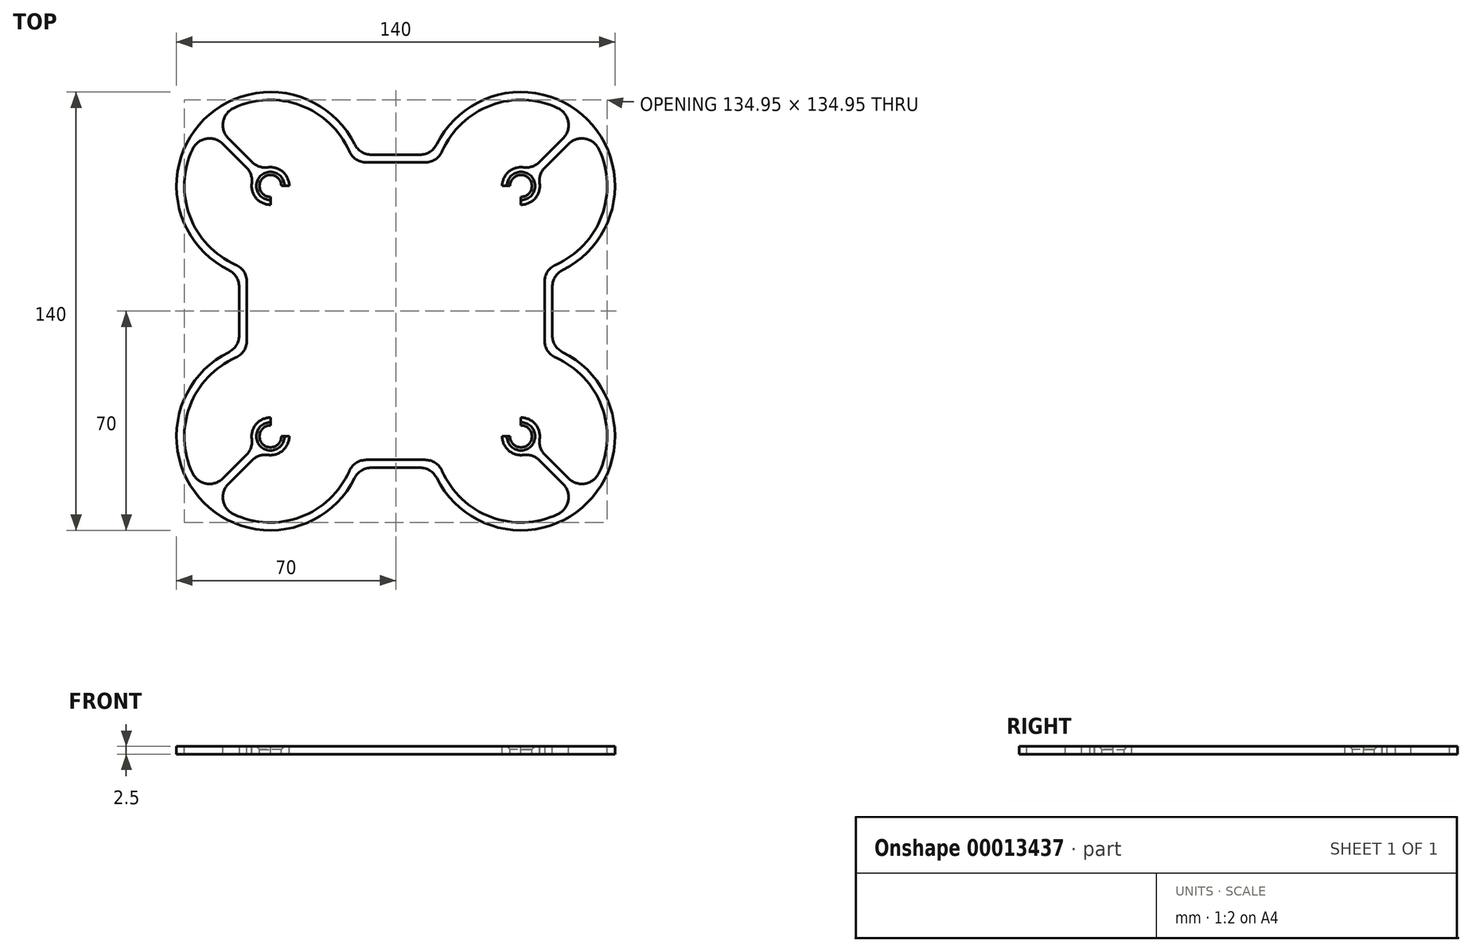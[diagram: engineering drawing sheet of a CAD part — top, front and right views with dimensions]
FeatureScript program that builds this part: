
annotation { "Feature Type Name" : "Feature", "Feature Type Description" : "" }
export const myFeature = defineFeature(function(context is Context, id is Id, definition is map)
    precondition{}
    {
        {
            var Q0;
            Q0=qCreatedBy(makeId("Top.planeOp"),FACE);
            var sketch = newSketch(context, id + "F0", { "sketchPlane" : qUnion([Q0])});
            skLineSegment(sketch, "E0.rect.bottom", {"start": v(40, 40) * mm, "end": v(-40, 40) * mm});
            skLineSegment(sketch, "E0.rect.top", {"start": v(40, -40) * mm, "end": v(-40, -40) * mm});
            skLineSegment(sketch, "E0.rect.left", {"start": v(40, 40) * mm, "end": v(40, -40) * mm});
            skLineSegment(sketch, "E0.rect.right", {"start": v(-40, 40) * mm, "end": v(-40, -40) * mm});
            skPoint(sketch, "E0.rect.middle", {"position": v(0, 0) * mm});
            skCircle(sketch, "E1", {"center": v(40, 40) * mm, "radius": 3.5 * mm});
            skCircle(sketch, "E2", {"center": v(-40, 40) * mm, "radius": 3.5 * mm});
            skCircle(sketch, "E3", {"center": v(-40, -40) * mm, "radius": 3.5 * mm});
            skCircle(sketch, "E4", {"center": v(40, -40) * mm, "radius": 3.5 * mm});
            skCircle(sketch, "E5", {"center": v(-40, -40) * mm, "radius": 30 * mm});
            skCircle(sketch, "E6", {"center": v(-40, 40) * mm, "radius": 30 * mm});
            skCircle(sketch, "E7", {"center": v(40, 40) * mm, "radius": 30 * mm});
            skCircle(sketch, "E8", {"center": v(40, -40) * mm, "radius": 30 * mm});
            skCircle(sketch, "E9", {"center": v(-40, 40) * mm, "radius": 27.5 * mm});
            skCircle(sketch, "E10", {"center": v(-40, -40) * mm, "radius": 27.5 * mm});
            skCircle(sketch, "E11", {"center": v(40, 40) * mm, "radius": 27.5 * mm});
            skCircle(sketch, "E12", {"center": v(40, -40) * mm, "radius": 27.5 * mm});
            skLineSegment(sketch, "E13", {"start": v(-40, 67.5) * mm, "end": v(-40, 70) * mm, "construction": true});
            skLineSegment(sketch, "E14", {"start": v(-40, -67.5) * mm, "end": v(-40, -70) * mm, "construction": true});
            skLineSegment(sketch, "E15", {"start": v(40, -67.5) * mm, "end": v(40, -70) * mm, "construction": true});
            skLineSegment(sketch, "E16", {"start": v(40, 67.5) * mm, "end": v(40, 70) * mm, "construction": true});
            skLineSegment(sketch, "E17.rect.bottom", {"start": v(50, 50) * mm, "end": v(-50, 50) * mm});
            skLineSegment(sketch, "E17.rect.top", {"start": v(50, -50) * mm, "end": v(-50, -50) * mm});
            skLineSegment(sketch, "E17.rect.left", {"start": v(50, 50) * mm, "end": v(50, -50) * mm});
            skLineSegment(sketch, "E17.rect.right", {"start": v(-50, 50) * mm, "end": v(-50, -50) * mm});
            skLineSegment(sketch, "E18.rect.bottom", {"start": v(47.5, 47.5) * mm, "end": v(-47.5, 47.5) * mm});
            skLineSegment(sketch, "E18.rect.top", {"start": v(47.5, -47.5) * mm, "end": v(-47.5, -47.5) * mm});
            skLineSegment(sketch, "E18.rect.left", {"start": v(47.5, 47.5) * mm, "end": v(47.5, -47.5) * mm});
            skLineSegment(sketch, "E18.rect.right", {"start": v(-47.5, 47.5) * mm, "end": v(-47.5, -47.5) * mm});
            skLineSegment(sketch, "E19", {"start": v(0, 47.5) * mm, "end": v(0, 50) * mm, "construction": true});
            skLineSegment(sketch, "E20", {"start": v(-40, -40) * mm, "end": v(-59.45, -59.45) * mm, "construction": true});
            skLineSegment(sketch, "E21", {"start": v(-60.3, -58.54) * mm, "end": v(-45.03, -43.27) * mm});
            skLineSegment(sketch, "E22", {"start": v(-52.67, -50.9) * mm, "end": v(-50.9, -52.67) * mm, "construction": true});
            skLineSegment(sketch, "E23", {"start": v(-40, 40) * mm, "end": v(-59.45, 59.45) * mm, "construction": true});
            skCircle(sketch, "E24", {"center": v(-40, -40) * mm, "radius": 6 * mm});
            skLineSegment(sketch, "E25", {"start": v(-43.5, -40) * mm, "end": v(-46, -40) * mm, "construction": true});
            skLineSegment(sketch, "E26", {"start": v(-43.27, -45.03) * mm, "end": v(-58.54, -60.3) * mm});
            skCircle(sketch, "E27", {"center": v(-40, 40) * mm, "radius": 6 * mm});
            skLineSegment(sketch, "E28", {"start": v(-40, 43.5) * mm, "end": v(-40, 46) * mm, "construction": true});
            skLineSegment(sketch, "E29", {"start": v(-45.03, 43.27) * mm, "end": v(-60.3, 58.54) * mm});
            skLineSegment(sketch, "E30", {"start": v(-43.27, 45.03) * mm, "end": v(-58.54, 60.3) * mm});
            skLineSegment(sketch, "E31", {"start": v(-52.67, 50.9) * mm, "end": v(-50.9, 52.67) * mm, "construction": true});
            skLineSegment(sketch, "E32", {"start": v(40, 40) * mm, "end": v(61.21, 61.21) * mm, "construction": true});
            skLineSegment(sketch, "E33", {"start": v(50.9, 52.67) * mm, "end": v(52.67, 50.9) * mm, "construction": true});
            skCircle(sketch, "E34", {"center": v(40, 40) * mm, "radius": 6 * mm});
            skLineSegment(sketch, "E35", {"start": v(40, 43.5) * mm, "end": v(40, 46) * mm, "construction": true});
            skLineSegment(sketch, "E36", {"start": v(45.03, 43.27) * mm, "end": v(60.3, 58.54) * mm});
            skLineSegment(sketch, "E37", {"start": v(43.27, 45.03) * mm, "end": v(58.54, 60.3) * mm});
            skCircle(sketch, "E38", {"center": v(40, -40) * mm, "radius": 6 * mm});
            skLineSegment(sketch, "E39", {"start": v(40, -43.5) * mm, "end": v(40, -46) * mm, "construction": true});
            skLineSegment(sketch, "E40", {"start": v(40, -40) * mm, "end": v(59.45, -59.45) * mm, "construction": true});
            skLineSegment(sketch, "E41", {"start": v(43.27, -45.03) * mm, "end": v(58.54, -60.3) * mm});
            skLineSegment(sketch, "E42", {"start": v(45.03, -43.27) * mm, "end": v(60.3, -58.54) * mm});
            skLineSegment(sketch, "E43", {"start": v(50.9, -52.67) * mm, "end": v(52.67, -50.9) * mm, "construction": true});
            skSolve(sketch);
        }
        {
            var Q0;
            {var subQ3=sQuery(id+"F0.wireOp",EDGE,"E6");var subQ5=sQuery(id+"F0.wireOp",EDGE,"E17.rect.bottom");var subQ7=makeQuery(id+"F0.imprint","INTERSECT",VERTEX,{"derivedFrom":[subQ3,subQ5]});Q0=makeQuery(id+"F0.imprint","IMPRINT",FACE,{"disambiguationData":[TD([[makeQuery(id+"F0.imprint","IMPRINT",EDGE,{"disambiguationData":[TD([[subQ7,-1.0]])],"derivedFrom":subQ3}),1.0]])]});}
            var Q1;
            {var subQ3=sQuery(id+"F0.wireOp",EDGE,"E5");var subQ5=sQuery(id+"F0.wireOp",EDGE,"E17.rect.right");var subQ7=makeQuery(id+"F0.imprint","INTERSECT",VERTEX,{"derivedFrom":[subQ3,subQ5]});Q1=makeQuery(id+"F0.imprint","IMPRINT",FACE,{"disambiguationData":[TD([[makeQuery(id+"F0.imprint","IMPRINT",EDGE,{"disambiguationData":[TD([[subQ7,1.0]])],"derivedFrom":subQ3}),-1.0]])]});}
            var Q2;
            {var subQ0=sQuery(id+"F0.wireOp",EDGE,"E17.rect.right");var subQ3=sQuery(id+"F0.wireOp",EDGE,"E6");var subQ4=makeQuery(id+"F0.imprint","INTERSECT",VERTEX,{"derivedFrom":[subQ3,subQ0]});Q2=makeQuery(id+"F0.imprint","IMPRINT",FACE,{"disambiguationData":[TD([[makeQuery(id+"F0.imprint","IMPRINT",EDGE,{"disambiguationData":[TD([[subQ4,-1.0]])],"derivedFrom":subQ3}),1.0]])]});}
            var Q3;
            {var subQ3=sQuery(id+"F0.wireOp",EDGE,"E6");var subQ5=sQuery(id+"F0.wireOp",EDGE,"E17.rect.bottom");var subQ7=makeQuery(id+"F0.imprint","INTERSECT",VERTEX,{"derivedFrom":[subQ3,subQ5]});Q3=makeQuery(id+"F0.imprint","IMPRINT",FACE,{"disambiguationData":[TD([[makeQuery(id+"F0.imprint","IMPRINT",EDGE,{"disambiguationData":[TD([[subQ7,1.0]])],"derivedFrom":subQ3}),1.0]])]});}
            var Q4;
            {var subQ1=sQuery(id+"F0.wireOp",EDGE,"E18.rect.bottom");var subQ6=sQuery(id+"F0.wireOp",EDGE,"E18.rect.right");var subQ9=makeQuery(id+"F0.imprint","INTERSECT",VERTEX,{"derivedFrom":[subQ1,subQ6]});Q4=makeQuery(id+"F0.imprint","IMPRINT",FACE,{"disambiguationData":[TD([[makeQuery(id+"F0.imprint","IMPRINT",EDGE,{"disambiguationData":[TD([[subQ9,1.0]])],"derivedFrom":subQ1}),1.0]])]});}
            var Q5;
            {var subQ3=sQuery(id+"F0.wireOp",EDGE,"E17.rect.bottom");var subQ8=sQuery(id+"F0.wireOp",EDGE,"E17.rect.right");var subQ11=makeQuery(id+"F0.imprint","INTERSECT",VERTEX,{"derivedFrom":[subQ3,subQ8]});Q5=makeQuery(id+"F0.imprint","IMPRINT",FACE,{"disambiguationData":[TD([[makeQuery(id+"F0.imprint","IMPRINT",EDGE,{"disambiguationData":[TD([[subQ11,1.0]])],"derivedFrom":subQ3}),1.0]])]});}
            var Q6;
            {var subQ0=sQuery(id+"F0.wireOp",EDGE,"E29");var subQ3=sQuery(id+"F0.wireOp",EDGE,"E9");var subQ4=makeQuery(id+"F0.imprint","INTERSECT",VERTEX,{"derivedFrom":[subQ3,subQ0]});Q6=makeQuery(id+"F0.imprint","IMPRINT",FACE,{"disambiguationData":[TD([[makeQuery(id+"F0.imprint","IMPRINT",EDGE,{"disambiguationData":[TD([[subQ4,1.0]])],"derivedFrom":subQ3}),1.0]])]});}
            var Q7;
            {var subQ3=sQuery(id+"F0.wireOp",EDGE,"E6");var subQ5=sQuery(id+"F0.wireOp",EDGE,"E17.rect.bottom");var subQ7=makeQuery(id+"F0.imprint","INTERSECT",VERTEX,{"derivedFrom":[subQ3,subQ5]});Q7=makeQuery(id+"F0.imprint","IMPRINT",FACE,{"disambiguationData":[TD([[makeQuery(id+"F0.imprint","IMPRINT",EDGE,{"disambiguationData":[TD([[subQ7,1.0]])],"derivedFrom":subQ3}),-1.0]])]});}
            var Q8;
            {var subQ3=sQuery(id+"F0.wireOp",EDGE,"E7");var subQ5=sQuery(id+"F0.wireOp",EDGE,"E17.rect.bottom");var subQ7=makeQuery(id+"F0.imprint","INTERSECT",VERTEX,{"derivedFrom":[subQ3,subQ5]});Q8=makeQuery(id+"F0.imprint","IMPRINT",FACE,{"disambiguationData":[TD([[makeQuery(id+"F0.imprint","IMPRINT",EDGE,{"disambiguationData":[TD([[subQ7,-1.0]])],"derivedFrom":subQ3}),1.0]])]});}
            var Q9;
            {var subQ3=sQuery(id+"F0.wireOp",EDGE,"E7");var subQ5=sQuery(id+"F0.wireOp",EDGE,"E17.rect.bottom");var subQ7=makeQuery(id+"F0.imprint","INTERSECT",VERTEX,{"derivedFrom":[subQ3,subQ5]});Q9=makeQuery(id+"F0.imprint","IMPRINT",FACE,{"disambiguationData":[TD([[makeQuery(id+"F0.imprint","IMPRINT",EDGE,{"disambiguationData":[TD([[subQ7,1.0]])],"derivedFrom":subQ3}),1.0]])]});}
            var Q10;
            {var subQ3=sQuery(id+"F0.wireOp",EDGE,"E11");var subQ5=sQuery(id+"F0.wireOp",EDGE,"E36");var subQ8=makeQuery(id+"F0.imprint","INTERSECT",VERTEX,{"derivedFrom":[subQ3,subQ5]});Q10=makeQuery(id+"F0.imprint","IMPRINT",FACE,{"disambiguationData":[TD([[makeQuery(id+"F0.imprint","IMPRINT",EDGE,{"disambiguationData":[TD([[subQ8,-1.0]])],"derivedFrom":subQ3}),1.0]])]});}
            var Q11;
            {var subQ3=sQuery(id+"F0.wireOp",EDGE,"E17.rect.bottom");var subQ8=sQuery(id+"F0.wireOp",EDGE,"E17.rect.left");var subQ11=makeQuery(id+"F0.imprint","INTERSECT",VERTEX,{"derivedFrom":[subQ3,subQ8]});Q11=makeQuery(id+"F0.imprint","IMPRINT",FACE,{"disambiguationData":[TD([[makeQuery(id+"F0.imprint","IMPRINT",EDGE,{"disambiguationData":[TD([[subQ11,-1.0]])],"derivedFrom":subQ3}),1.0]])]});}
            var Q12;
            {var subQ1=sQuery(id+"F0.wireOp",EDGE,"E18.rect.bottom");var subQ6=sQuery(id+"F0.wireOp",EDGE,"E18.rect.left");var subQ9=makeQuery(id+"F0.imprint","INTERSECT",VERTEX,{"derivedFrom":[subQ1,subQ6]});Q12=makeQuery(id+"F0.imprint","IMPRINT",FACE,{"disambiguationData":[TD([[makeQuery(id+"F0.imprint","IMPRINT",EDGE,{"disambiguationData":[TD([[subQ9,-1.0]])],"derivedFrom":subQ1}),1.0]])]});}
            var Q13;
            {var subQ3=sQuery(id+"F0.wireOp",EDGE,"E7");var subQ5=sQuery(id+"F0.wireOp",EDGE,"E17.rect.left");var subQ7=makeQuery(id+"F0.imprint","INTERSECT",VERTEX,{"derivedFrom":[subQ3,subQ5]});Q13=makeQuery(id+"F0.imprint","IMPRINT",FACE,{"disambiguationData":[TD([[makeQuery(id+"F0.imprint","IMPRINT",EDGE,{"disambiguationData":[TD([[subQ7,1.0]])],"derivedFrom":subQ3}),-1.0]])]});}
            var Q14;
            {var subQ3=sQuery(id+"F0.wireOp",EDGE,"E8");var subQ5=sQuery(id+"F0.wireOp",EDGE,"E17.rect.left");var subQ7=makeQuery(id+"F0.imprint","INTERSECT",VERTEX,{"derivedFrom":[subQ3,subQ5]});Q14=makeQuery(id+"F0.imprint","IMPRINT",FACE,{"disambiguationData":[TD([[makeQuery(id+"F0.imprint","IMPRINT",EDGE,{"disambiguationData":[TD([[subQ7,-1.0]])],"derivedFrom":subQ3}),1.0]])]});}
            var Q15;
            {var subQ0=sQuery(id+"F0.wireOp",EDGE,"E17.rect.left");var subQ3=sQuery(id+"F0.wireOp",EDGE,"E7");var subQ4=makeQuery(id+"F0.imprint","INTERSECT",VERTEX,{"derivedFrom":[subQ3,subQ0]});Q15=makeQuery(id+"F0.imprint","IMPRINT",FACE,{"disambiguationData":[TD([[makeQuery(id+"F0.imprint","IMPRINT",EDGE,{"disambiguationData":[TD([[subQ4,1.0]])],"derivedFrom":subQ3}),1.0]])]});}
            var Q16;
            {var subQ3=sQuery(id+"F0.wireOp",EDGE,"E17.rect.left");var subQ8=sQuery(id+"F0.wireOp",EDGE,"E17.rect.top");var subQ11=makeQuery(id+"F0.imprint","INTERSECT",VERTEX,{"derivedFrom":[subQ8,subQ3]});Q16=makeQuery(id+"F0.imprint","IMPRINT",FACE,{"disambiguationData":[TD([[makeQuery(id+"F0.imprint","IMPRINT",EDGE,{"disambiguationData":[TD([[subQ11,-1.0]])],"derivedFrom":subQ8}),-1.0]])]});}
            var Q17;
            {var subQ0=sQuery(id+"F0.wireOp",EDGE,"E17.rect.left");var subQ3=sQuery(id+"F0.wireOp",EDGE,"E8");var subQ4=makeQuery(id+"F0.imprint","INTERSECT",VERTEX,{"derivedFrom":[subQ3,subQ0]});Q17=makeQuery(id+"F0.imprint","IMPRINT",FACE,{"disambiguationData":[TD([[makeQuery(id+"F0.imprint","IMPRINT",EDGE,{"disambiguationData":[TD([[subQ4,1.0]])],"derivedFrom":subQ3}),1.0]])]});}
            var Q18;
            {var subQ3=sQuery(id+"F0.wireOp",EDGE,"E12");var subQ5=sQuery(id+"F0.wireOp",EDGE,"E41");var subQ8=makeQuery(id+"F0.imprint","INTERSECT",VERTEX,{"derivedFrom":[subQ3,subQ5]});Q18=makeQuery(id+"F0.imprint","IMPRINT",FACE,{"disambiguationData":[TD([[makeQuery(id+"F0.imprint","IMPRINT",EDGE,{"disambiguationData":[TD([[subQ8,-1.0]])],"derivedFrom":subQ3}),1.0]])]});}
            var Q19;
            {var subQ1=sQuery(id+"F0.wireOp",EDGE,"E18.rect.left");var subQ6=sQuery(id+"F0.wireOp",EDGE,"E18.rect.top");var subQ9=makeQuery(id+"F0.imprint","INTERSECT",VERTEX,{"derivedFrom":[subQ6,subQ1]});Q19=makeQuery(id+"F0.imprint","IMPRINT",FACE,{"disambiguationData":[TD([[makeQuery(id+"F0.imprint","IMPRINT",EDGE,{"disambiguationData":[TD([[subQ9,-1.0]])],"derivedFrom":subQ6}),-1.0]])]});}
            var Q20;
            {var subQ3=sQuery(id+"F0.wireOp",EDGE,"E8");var subQ5=sQuery(id+"F0.wireOp",EDGE,"E17.rect.top");var subQ7=makeQuery(id+"F0.imprint","INTERSECT",VERTEX,{"derivedFrom":[subQ3,subQ5]});Q20=makeQuery(id+"F0.imprint","IMPRINT",FACE,{"disambiguationData":[TD([[makeQuery(id+"F0.imprint","IMPRINT",EDGE,{"disambiguationData":[TD([[subQ7,1.0]])],"derivedFrom":subQ3}),1.0]])]});}
            var Q21;
            {var subQ3=sQuery(id+"F0.wireOp",EDGE,"E5");var subQ5=sQuery(id+"F0.wireOp",EDGE,"E17.rect.top");var subQ7=makeQuery(id+"F0.imprint","INTERSECT",VERTEX,{"derivedFrom":[subQ3,subQ5]});Q21=makeQuery(id+"F0.imprint","IMPRINT",FACE,{"disambiguationData":[TD([[makeQuery(id+"F0.imprint","IMPRINT",EDGE,{"disambiguationData":[TD([[subQ7,-1.0]])],"derivedFrom":subQ3}),-1.0]])]});}
            var Q22;
            {var subQ3=sQuery(id+"F0.wireOp",EDGE,"E5");var subQ5=sQuery(id+"F0.wireOp",EDGE,"E17.rect.top");var subQ7=makeQuery(id+"F0.imprint","INTERSECT",VERTEX,{"derivedFrom":[subQ3,subQ5]});Q22=makeQuery(id+"F0.imprint","IMPRINT",FACE,{"disambiguationData":[TD([[makeQuery(id+"F0.imprint","IMPRINT",EDGE,{"disambiguationData":[TD([[subQ7,-1.0]])],"derivedFrom":subQ3}),1.0]])]});}
            var Q23;
            {var subQ3=sQuery(id+"F0.wireOp",EDGE,"E5");var subQ6=sQuery(id+"F0.wireOp",EDGE,"E17.rect.right");var subQ8=makeQuery(id+"F0.imprint","INTERSECT",VERTEX,{"derivedFrom":[subQ3,subQ6]});Q23=makeQuery(id+"F0.imprint","IMPRINT",FACE,{"disambiguationData":[TD([[makeQuery(id+"F0.imprint","IMPRINT",EDGE,{"disambiguationData":[TD([[subQ8,-1.0]])],"derivedFrom":subQ3}),1.0]])]});}
            var Q24;
            {var subQ3=sQuery(id+"F0.wireOp",EDGE,"E10");var subQ5=sQuery(id+"F0.wireOp",EDGE,"E21");var subQ8=makeQuery(id+"F0.imprint","INTERSECT",VERTEX,{"derivedFrom":[subQ3,subQ5]});Q24=makeQuery(id+"F0.imprint","IMPRINT",FACE,{"disambiguationData":[TD([[makeQuery(id+"F0.imprint","IMPRINT",EDGE,{"disambiguationData":[TD([[subQ8,-1.0]])],"derivedFrom":subQ3}),1.0]])]});}
            var Q25;
            {var subQ3=sQuery(id+"F0.wireOp",EDGE,"E17.rect.right");var subQ8=sQuery(id+"F0.wireOp",EDGE,"E17.rect.top");var subQ11=makeQuery(id+"F0.imprint","INTERSECT",VERTEX,{"derivedFrom":[subQ8,subQ3]});Q25=makeQuery(id+"F0.imprint","IMPRINT",FACE,{"disambiguationData":[TD([[makeQuery(id+"F0.imprint","IMPRINT",EDGE,{"disambiguationData":[TD([[subQ11,1.0]])],"derivedFrom":subQ8}),-1.0]])]});}
            var Q26;
            {var subQ1=sQuery(id+"F0.wireOp",EDGE,"E18.rect.top");var subQ7=sQuery(id+"F0.wireOp",EDGE,"E18.rect.right");var subQ9=makeQuery(id+"F0.imprint","INTERSECT",VERTEX,{"derivedFrom":[subQ1,subQ7]});Q26=makeQuery(id+"F0.imprint","IMPRINT",FACE,{"disambiguationData":[TD([[makeQuery(id+"F0.imprint","IMPRINT",EDGE,{"disambiguationData":[TD([[subQ9,1.0]])],"derivedFrom":subQ1}),-1.0]])]});}
            var Q27;
            {var subQ3=sQuery(id+"F0.wireOp",EDGE,"E5");var subQ5=sQuery(id+"F0.wireOp",EDGE,"E17.rect.right");var subQ7=makeQuery(id+"F0.imprint","INTERSECT",VERTEX,{"derivedFrom":[subQ3,subQ5]});Q27=makeQuery(id+"F0.imprint","IMPRINT",FACE,{"disambiguationData":[TD([[makeQuery(id+"F0.imprint","IMPRINT",EDGE,{"disambiguationData":[TD([[subQ7,1.0]])],"derivedFrom":subQ3}),1.0]])]});}
            var Q28;
            {var subQ0=sQuery(id+"F0.wireOp",EDGE,"E27");var subQ5=sQuery(id+"F0.wireOp",EDGE,"E0.rect.bottom");var subQ6=makeQuery(id+"F0.imprint","INTERSECT",VERTEX,{"derivedFrom":[subQ5,subQ0]});Q28=makeQuery(id+"F0.imprint","IMPRINT",FACE,{"disambiguationData":[TD([[makeQuery(id+"F0.imprint","IMPRINT",EDGE,{"disambiguationData":[TD([[subQ6,-1.0]])],"derivedFrom":subQ5}),-1.0]])]});}
            var Q29;
            {var subQ4=sQuery(id+"F0.wireOp",EDGE,"E0.rect.bottom");var subQ7=sQuery(id+"F0.wireOp",EDGE,"E1");var subQ9=makeQuery(id+"F0.imprint","INTERSECT",VERTEX,{"derivedFrom":[subQ4,subQ7]});Q29=makeQuery(id+"F0.imprint","IMPRINT",FACE,{"disambiguationData":[TD([[makeQuery(id+"F0.imprint","IMPRINT",EDGE,{"disambiguationData":[TD([[subQ9,-1.0]])],"derivedFrom":subQ4}),-1.0]])]});}
            var Q30;
            {var subQ3=sQuery(id+"F0.wireOp",EDGE,"E0.rect.top");var subQ5=sQuery(id+"F0.wireOp",EDGE,"E4");var subQ8=makeQuery(id+"F0.imprint","INTERSECT",VERTEX,{"derivedFrom":[subQ3,subQ5]});Q30=makeQuery(id+"F0.imprint","IMPRINT",FACE,{"disambiguationData":[TD([[makeQuery(id+"F0.imprint","IMPRINT",EDGE,{"disambiguationData":[TD([[subQ8,-1.0]])],"derivedFrom":subQ3}),1.0]])]});}
            var Q31;
            {var subQ0=sQuery(id+"F0.wireOp",EDGE,"E24");var subQ1=sQuery(id+"F0.wireOp",EDGE,"E0.rect.top");var subQ2=makeQuery(id+"F0.imprint","INTERSECT",VERTEX,{"derivedFrom":[subQ1,subQ0]});Q31=makeQuery(id+"F0.imprint","IMPRINT",FACE,{"disambiguationData":[TD([[makeQuery(id+"F0.imprint","IMPRINT",EDGE,{"disambiguationData":[TD([[subQ2,-1.0]])],"derivedFrom":subQ1}),1.0]])]});}
            extrude(context, id + "F1", {"entities" : qUnion([Q0, Q1, Q2, Q3, Q4, Q5, Q6, Q7, Q8, Q9, Q10, Q11, Q12, Q13, Q14, Q15, Q16, Q17, Q18, Q19, Q20, Q21, Q22, Q23, Q24, Q25, Q26, Q27, Q28, Q29, Q30, Q31]), "oppositeDirection" : true, "depth" : 2.5 * mm});
        }
        {
            var Q0;
            Q0=makeQuery(id+"F1.opExtrude","SWEPT_EDGE",EDGE,{"disambiguationData":[OSD([sQuery(id+"F0.wireOp",EDGE,"E9"),sQuery(id+"F0.wireOp",EDGE,"E29")])]});
            var Q1;
            Q1=makeQuery(id+"F1.opExtrude","SWEPT_EDGE",EDGE,{"disambiguationData":[OSD([sQuery(id+"F0.wireOp",EDGE,"E9"),sQuery(id+"F0.wireOp",EDGE,"E30")])]});
            var Q2;
            Q2=makeQuery(id+"F1.opExtrude","SWEPT_EDGE",EDGE,{"disambiguationData":[OSD([sQuery(id+"F0.wireOp",EDGE,"E10"),sQuery(id+"F0.wireOp",EDGE,"E18.rect.right")])]});
            var Q3;
            Q3=makeQuery(id+"F1.opExtrude","SWEPT_EDGE",EDGE,{"disambiguationData":[OSD([sQuery(id+"F0.wireOp",EDGE,"E5"),sQuery(id+"F0.wireOp",EDGE,"E17.rect.right")])]});
            var Q4;
            Q4=makeQuery(id+"F1.opExtrude","SWEPT_EDGE",EDGE,{"disambiguationData":[OSD([sQuery(id+"F0.wireOp",EDGE,"E6"),sQuery(id+"F0.wireOp",EDGE,"E17.rect.right")])]});
            var Q5;
            Q5=makeQuery(id+"F1.opExtrude","SWEPT_EDGE",EDGE,{"disambiguationData":[OSD([sQuery(id+"F0.wireOp",EDGE,"E9"),sQuery(id+"F0.wireOp",EDGE,"E18.rect.right")])]});
            var Q6;
            Q6=makeQuery(id+"F1.opExtrude","SWEPT_EDGE",EDGE,{"disambiguationData":[OSD([sQuery(id+"F0.wireOp",EDGE,"E10"),sQuery(id+"F0.wireOp",EDGE,"E26")])]});
            var Q7;
            Q7=makeQuery(id+"F1.opExtrude","SWEPT_EDGE",EDGE,{"disambiguationData":[OSD([sQuery(id+"F0.wireOp",EDGE,"E10"),sQuery(id+"F0.wireOp",EDGE,"E21")])]});
            var Q8;
            Q8=makeQuery(id+"F1.opExtrude","SWEPT_EDGE",EDGE,{"disambiguationData":[OSD([sQuery(id+"F0.wireOp",EDGE,"E10"),sQuery(id+"F0.wireOp",EDGE,"E18.rect.top")])]});
            var Q9;
            Q9=makeQuery(id+"F1.opExtrude","SWEPT_EDGE",EDGE,{"disambiguationData":[OSD([sQuery(id+"F0.wireOp",EDGE,"E12"),sQuery(id+"F0.wireOp",EDGE,"E18.rect.top")])]});
            var Q10;
            Q10=makeQuery(id+"F1.opExtrude","SWEPT_EDGE",EDGE,{"disambiguationData":[OSD([sQuery(id+"F0.wireOp",EDGE,"E5"),sQuery(id+"F0.wireOp",EDGE,"E17.rect.top")])]});
            var Q11;
            Q11=makeQuery(id+"F1.opExtrude","SWEPT_EDGE",EDGE,{"disambiguationData":[OSD([sQuery(id+"F0.wireOp",EDGE,"E8"),sQuery(id+"F0.wireOp",EDGE,"E17.rect.top")])]});
            var Q12;
            Q12=makeQuery(id+"F1.opExtrude","SWEPT_EDGE",EDGE,{"disambiguationData":[OSD([sQuery(id+"F0.wireOp",EDGE,"E12"),sQuery(id+"F0.wireOp",EDGE,"E42")])]});
            var Q13;
            Q13=makeQuery(id+"F1.opExtrude","SWEPT_EDGE",EDGE,{"disambiguationData":[OSD([sQuery(id+"F0.wireOp",EDGE,"E12"),sQuery(id+"F0.wireOp",EDGE,"E41")])]});
            var Q14;
            Q14=makeQuery(id+"F1.opExtrude","SWEPT_EDGE",EDGE,{"disambiguationData":[OSD([sQuery(id+"F0.wireOp",EDGE,"E11"),sQuery(id+"F0.wireOp",EDGE,"E18.rect.left")])]});
            var Q15;
            Q15=makeQuery(id+"F1.opExtrude","SWEPT_EDGE",EDGE,{"disambiguationData":[OSD([sQuery(id+"F0.wireOp",EDGE,"E12"),sQuery(id+"F0.wireOp",EDGE,"E18.rect.left")])]});
            var Q16;
            Q16=makeQuery(id+"F1.opExtrude","SWEPT_EDGE",EDGE,{"disambiguationData":[OSD([sQuery(id+"F0.wireOp",EDGE,"E8"),sQuery(id+"F0.wireOp",EDGE,"E17.rect.left")])]});
            var Q17;
            Q17=makeQuery(id+"F1.opExtrude","SWEPT_EDGE",EDGE,{"disambiguationData":[OSD([sQuery(id+"F0.wireOp",EDGE,"E7"),sQuery(id+"F0.wireOp",EDGE,"E17.rect.left")])]});
            var Q18;
            Q18=makeQuery(id+"F1.opExtrude","SWEPT_EDGE",EDGE,{"disambiguationData":[OSD([sQuery(id+"F0.wireOp",EDGE,"E11"),sQuery(id+"F0.wireOp",EDGE,"E36")])]});
            var Q19;
            Q19=makeQuery(id+"F1.opExtrude","SWEPT_EDGE",EDGE,{"disambiguationData":[OSD([sQuery(id+"F0.wireOp",EDGE,"E11"),sQuery(id+"F0.wireOp",EDGE,"E37")])]});
            var Q20;
            Q20=makeQuery(id+"F1.opExtrude","SWEPT_EDGE",EDGE,{"disambiguationData":[OSD([sQuery(id+"F0.wireOp",EDGE,"E11"),sQuery(id+"F0.wireOp",EDGE,"E18.rect.bottom")])]});
            var Q21;
            Q21=makeQuery(id+"F1.opExtrude","SWEPT_EDGE",EDGE,{"disambiguationData":[OSD([sQuery(id+"F0.wireOp",EDGE,"E9"),sQuery(id+"F0.wireOp",EDGE,"E18.rect.bottom")])]});
            var Q22;
            Q22=makeQuery(id+"F1.opExtrude","SWEPT_EDGE",EDGE,{"disambiguationData":[OSD([sQuery(id+"F0.wireOp",EDGE,"E6"),sQuery(id+"F0.wireOp",EDGE,"E17.rect.bottom")])]});
            var Q23;
            Q23=makeQuery(id+"F1.opExtrude","SWEPT_EDGE",EDGE,{"disambiguationData":[OSD([sQuery(id+"F0.wireOp",EDGE,"E7"),sQuery(id+"F0.wireOp",EDGE,"E17.rect.bottom")])]});
            var Q24;
            Q24=makeQuery(id+"F1.opExtrude","SWEPT_EDGE",EDGE,{"disambiguationData":[OSD([sQuery(id+"F0.wireOp",EDGE,"E24"),sQuery(id+"F0.wireOp",EDGE,"E26")])]});
            var Q25;
            Q25=makeQuery(id+"F1.opExtrude","SWEPT_EDGE",EDGE,{"disambiguationData":[OSD([sQuery(id+"F0.wireOp",EDGE,"E21"),sQuery(id+"F0.wireOp",EDGE,"E24")])]});
            var Q26;
            Q26=makeQuery(id+"F1.opExtrude","SWEPT_EDGE",EDGE,{"disambiguationData":[OSD([sQuery(id+"F0.wireOp",EDGE,"E38"),sQuery(id+"F0.wireOp",EDGE,"E41")])]});
            var Q27;
            Q27=makeQuery(id+"F1.opExtrude","SWEPT_EDGE",EDGE,{"disambiguationData":[OSD([sQuery(id+"F0.wireOp",EDGE,"E38"),sQuery(id+"F0.wireOp",EDGE,"E42")])]});
            var Q28;
            Q28=makeQuery(id+"F1.opExtrude","SWEPT_EDGE",EDGE,{"disambiguationData":[OSD([sQuery(id+"F0.wireOp",EDGE,"E34"),sQuery(id+"F0.wireOp",EDGE,"E36")])]});
            var Q29;
            Q29=makeQuery(id+"F1.opExtrude","SWEPT_EDGE",EDGE,{"disambiguationData":[OSD([sQuery(id+"F0.wireOp",EDGE,"E34"),sQuery(id+"F0.wireOp",EDGE,"E37")])]});
            var Q30;
            Q30=makeQuery(id+"F1.opExtrude","SWEPT_EDGE",EDGE,{"disambiguationData":[OSD([sQuery(id+"F0.wireOp",EDGE,"E27"),sQuery(id+"F0.wireOp",EDGE,"E30")])]});
            var Q31;
            Q31=makeQuery(id+"F1.opExtrude","SWEPT_EDGE",EDGE,{"disambiguationData":[OSD([sQuery(id+"F0.wireOp",EDGE,"E27"),sQuery(id+"F0.wireOp",EDGE,"E29")])]});
            fillet(context, id + "F2", {"entities" : qUnion([Q0, Q1, Q2, Q3, Q4, Q5, Q6, Q7, Q8, Q9, Q10, Q11, Q12, Q13, Q14, Q15, Q16, Q17, Q18, Q19, Q20, Q21, Q22, Q23, Q24, Q25, Q26, Q27, Q28, Q29, Q30, Q31]), "radius" : 6 * mm, "tangentPropagation" : true, "allowEdgeOverflow" : false});
        }
        {
            var Q0;
            Q0=makeQuery(id+"F1.opExtrude","CAP_EDGE",EDGE,{"disambiguationData":[OSD([sQuery(id+"F0.wireOp",EDGE,"E3")])],"isStart":true});
            var Q1;
            Q1=makeQuery(id+"F1.opExtrude","CAP_EDGE",EDGE,{"disambiguationData":[OSD([sQuery(id+"F0.wireOp",EDGE,"E2")])],"isStart":true});
            var Q2;
            Q2=makeQuery(id+"F1.opExtrude","CAP_EDGE",EDGE,{"disambiguationData":[OSD([sQuery(id+"F0.wireOp",EDGE,"E4")])],"isStart":true});
            var Q3;
            Q3=makeQuery(id+"F1.opExtrude","CAP_EDGE",EDGE,{"disambiguationData":[OSD([sQuery(id+"F0.wireOp",EDGE,"E1")])],"isStart":true});
            chamfer(context, id + "F3", {"entities" : qUnion([Q0, Q1, Q2, Q3]), "width" : 1 * mm, "tangentPropagation" : true});
        }
    });
